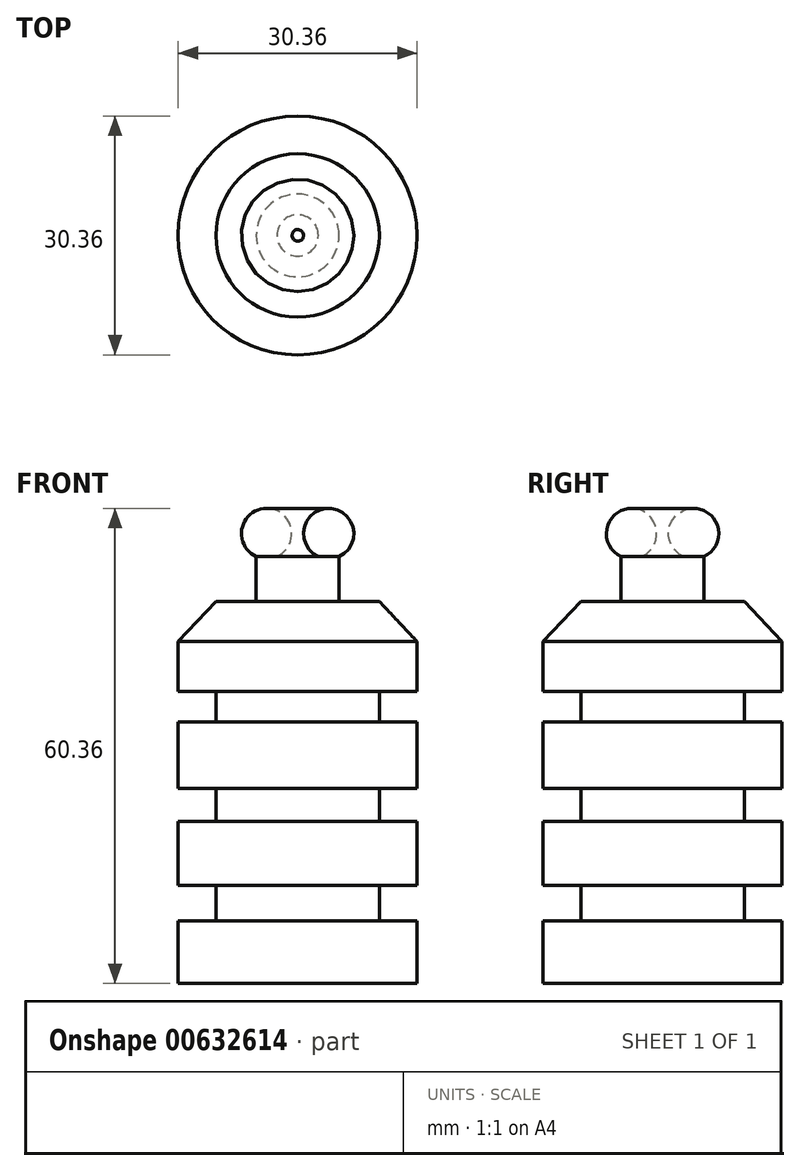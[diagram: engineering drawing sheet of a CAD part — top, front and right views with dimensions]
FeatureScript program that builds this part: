
annotation { "Feature Type Name" : "Feature", "Feature Type Description" : "" }
export const myFeature = defineFeature(function(context is Context, id is Id, definition is map)
    precondition{}
    {
        {
            var Q0;
            Q0=qCreatedBy(makeId("Front.planeOp"),FACE);
            var sketch = newSketch(context, id + "F0", { "sketchPlane" : qUnion([Q0])});
            skLineSegment(sketch, "E0", {"start": v(0, 0) * mm, "end": v(15.18, 0) * mm});
            skLineSegment(sketch, "E1", {"start": v(15.18, 0) * mm, "end": v(15.18, 7.97) * mm});
            skLineSegment(sketch, "E2", {"start": v(15.18, 7.97) * mm, "end": v(10.37, 7.97) * mm});
            skLineSegment(sketch, "E3", {"start": v(10.37, 7.97) * mm, "end": v(10.37, 12.47) * mm});
            skLineSegment(sketch, "E4", {"start": v(10.37, 12.47) * mm, "end": v(15.18, 12.47) * mm});
            skLineSegment(sketch, "E5", {"start": v(15.18, 12.47) * mm, "end": v(15.18, 20.59) * mm});
            skLineSegment(sketch, "E6", {"start": v(15.18, 20.59) * mm, "end": v(10.37, 20.59) * mm});
            skLineSegment(sketch, "E7", {"start": v(10.37, 20.59) * mm, "end": v(10.37, 24.8) * mm});
            skLineSegment(sketch, "E8", {"start": v(10.37, 24.8) * mm, "end": v(15.18, 24.8) * mm});
            skLineSegment(sketch, "E9", {"start": v(15.18, 24.8) * mm, "end": v(15.18, 33.21) * mm});
            skLineSegment(sketch, "E10", {"start": v(15.18, 33.21) * mm, "end": v(10.37, 33.21) * mm});
            skLineSegment(sketch, "E11", {"start": v(10.37, 33.21) * mm, "end": v(10.37, 37.12) * mm});
            skLineSegment(sketch, "E12", {"start": v(10.37, 37.12) * mm, "end": v(15.18, 37.12) * mm});
            skLineSegment(sketch, "E13", {"start": v(15.18, 37.12) * mm, "end": v(15.18, 43.43) * mm});
            skLineSegment(sketch, "E14", {"start": v(15.18, 43.43) * mm, "end": v(10.37, 48.54) * mm});
            skLineSegment(sketch, "E15", {"start": v(10.37, 48.54) * mm, "end": v(5.26, 48.54) * mm});
            skLineSegment(sketch, "E16", {"start": v(5.26, 48.54) * mm, "end": v(5.26, 54.25) * mm});
            skLineSegment(sketch, "E17", {"start": v(5.26, 54.25) * mm, "end": v(0, 54.25) * mm});
            skLineSegment(sketch, "E18", {"start": v(0, 54.25) * mm, "end": v(0, 0) * mm});
            skArc(sketch, "E19", {"start": v(5.26, 54.25) * mm, "mid": v(3.95, 60.36) * mm, "end": v(2.63, 54.25) * mm});
            skLineSegment(sketch, "E20", {"start": v(5.26, 54.25) * mm, "end": v(14.3, 54.25) * mm});
            skLineSegment(sketch, "E21", {"start": v(14.3, 54.25) * mm, "end": v(14.3, 44.36) * mm});
            skSolve(sketch);
        }
        {
            var Q0;
            Q0=makeQuery(id+"F0.imprint","IMPRINT",FACE,{"disambiguationData":[TD([[makeQuery(id+"F0.imprint","IMPRINT",EDGE,{"derivedFrom":sQuery(id+"F0.wireOp",EDGE,"E0")}),1.0]])]});
            var Q1;
            {var subQ0=sQuery(id+"F0.wireOp",EDGE,"E19");Q1=makeQuery(id+"F0.imprint","IMPRINT",FACE,{"disambiguationData":[TD([[makeQuery(id+"F0.imprint","IMPRINT",EDGE,{"derivedFrom":subQ0}),1.0]])]});}
            var Q2;
            Q2=sQuery(id+"F0.wireOp",EDGE,"E18");
            revolve(context, id + "F1", {"entities" : qUnion([Q0, Q1]), "axis" : qUnion([Q2]), "revolveType" : RevolveType.FULL});
        }
    });
